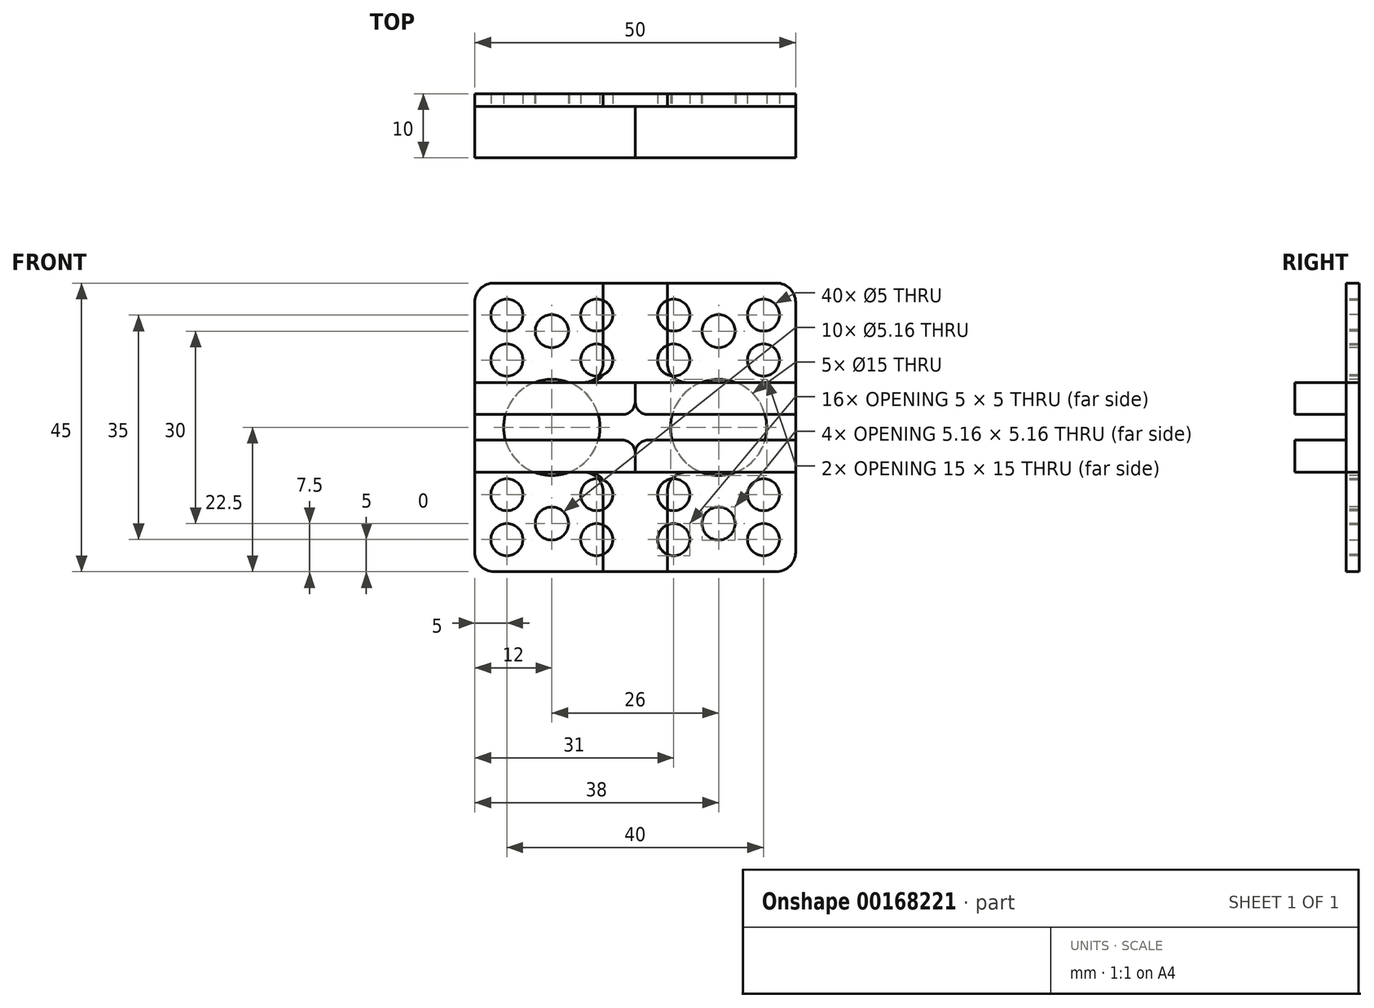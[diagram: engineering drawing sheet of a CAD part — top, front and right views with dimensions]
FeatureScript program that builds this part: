
annotation { "Feature Type Name" : "Feature", "Feature Type Description" : "" }
export const myFeature = defineFeature(function(context is Context, id is Id, definition is map)
    precondition{}
    {
        {
            var Q0;
            Q0=qCreatedBy(makeId("Top.planeOp"),FACE);
            var sketch = newSketch(context, id + "F0", { "sketchPlane" : qUnion([Q0])});
            skLineSegment(sketch, "E0.bottom", {"start": v(-25, -5) * mm, "end": v(25, -5) * mm});
            skLineSegment(sketch, "E0.top", {"start": v(-25, 5) * mm, "end": v(25, 5) * mm});
            skLineSegment(sketch, "E0.left", {"start": v(-25, -5) * mm, "end": v(-25, 5) * mm});
            skLineSegment(sketch, "E0.right", {"start": v(25, -5) * mm, "end": v(25, 5) * mm});
            skPoint(sketch, "E0.middle", {"position": v(0, 0) * mm});
            skSolve(sketch);
        }
        {
            var Q0;
            Q0 = qSketchRegion(id + "F0", true);
            extrude(context, id + "F1", {"entities" : qUnion([Q0]), "depth" : 45 * mm, "offsetDistance" : 25 * mm});
        }
        {
            var Q0;
            Q0=makeQuery(id+"F1.opExtrude","SWEPT_FACE",FACE,{"disambiguationData":[OSD([sQuery(id+"F0.wireOp",EDGE,"E0.bottom")])]});
            var sketch = newSketch(context, id + "F2", { "sketchPlane" : qUnion([Q0])});
            skCircle(sketch, "E1", {"center": v(13, 37.5) * mm, "radius": 2.58 * mm});
            skCircle(sketch, "E2", {"center": v(13, 7.5) * mm, "radius": 2.58 * mm});
            skLineSegment(sketch, "E3", {"start": v(13, 7.5) * mm, "end": v(13, 37.5) * mm, "construction": true});
            skLineSegment(sketch, "E4", {"start": v(13, 22.5) * mm, "end": v(25, 22.5) * mm, "construction": true});
            skSolve(sketch);
        }
        {
            var Q0;
            Q0 = qSketchRegion(id + "F2", true);
            extrude(context, id + "F3", {"entities" : qUnion([Q0]), "operationType" : NewBodyOperationType.REMOVE, "oppositeDirection" : true, "depth" : 25 * mm, "offsetDistance" : 25 * mm});
        }
        {
            var Q0;
            Q0=makeQuery(id+"F1.opExtrude","SWEPT_FACE",FACE,{"disambiguationData":[OSD([sQuery(id+"F0.wireOp",EDGE,"E0.bottom")])]});
            var sketch = newSketch(context, id + "F4", { "sketchPlane" : qUnion([Q0])});
            skCircle(sketch, "E5", {"center": v(13, 22.5) * mm, "radius": 7.5 * mm});
            skLineSegment(sketch, "E6", {"start": v(13, 7.5) * mm, "end": v(13, 22.5) * mm, "construction": true});
            skLineSegment(sketch, "E7", {"start": v(13, 37.5) * mm, "end": v(13, 22.5) * mm, "construction": true});
            skSolve(sketch);
        }
        {
            var Q0;
            Q0 = qSketchRegion(id + "F4", true);
            extrude(context, id + "F5", {"entities" : qUnion([Q0]), "operationType" : NewBodyOperationType.REMOVE, "endBound" : BoundingType.THROUGH_ALL, "oppositeDirection" : true, "depth" : 25 * mm, "offsetDistance" : 25 * mm});
        }
        {
            var Q0;
            Q0=makeQuery(id+"F1.opExtrude","SWEPT_FACE",FACE,{"disambiguationData":[OSD([sQuery(id+"F0.wireOp",EDGE,"E0.bottom")])]});
            var sketch = newSketch(context, id + "F6", { "sketchPlane" : qUnion([Q0])});
            skCircle(sketch, "E8", {"center": v(6, 5) * mm, "radius": 2.5 * mm});
            skLineSegment(sketch, "E9", {"start": v(13, 22.5) * mm, "end": v(-10.41, 22.5) * mm, "construction": true});
            skLineSegment(sketch, "E10", {"start": v(13, 22.5) * mm, "end": v(13, -17.77) * mm, "construction": true});
            skCircle(sketch, "E11.MirrorC", {"center": v(6, 40) * mm, "radius": 2.5 * mm});
            skCircle(sketch, "E12.MirrorC", {"center": v(20, 5) * mm, "radius": 2.5 * mm});
            skCircle(sketch, "E13.MirrorC", {"center": v(20, 40) * mm, "radius": 2.5 * mm});
            skCircle(sketch, "E14", {"center": v(6, 12) * mm, "radius": 2.5 * mm});
            skCircle(sketch, "E15.MirrorC", {"center": v(6, 33) * mm, "radius": 2.5 * mm});
            skCircle(sketch, "E16.MirrorC", {"center": v(20, 12) * mm, "radius": 2.5 * mm});
            skCircle(sketch, "E17.MirrorC", {"center": v(20, 33) * mm, "radius": 2.5 * mm});
            skSolve(sketch);
        }
        {
            var Q0;
            Q0 = qSketchRegion(id + "F6", true);
            extrude(context, id + "F7", {"entities" : qUnion([Q0]), "operationType" : NewBodyOperationType.REMOVE, "oppositeDirection" : true, "depth" : 25 * mm, "offsetDistance" : 25 * mm});
        }
        {
            var Q0;
            Q0=makeQuery(id+"F1.opExtrude","SWEPT_FACE",FACE,{"disambiguationData":[OSD([sQuery(id+"F0.wireOp",EDGE,"E0.bottom")])]});
            var sketch = newSketch(context, id + "F8", { "sketchPlane" : qUnion([Q0])});
            skLineSegment(sketch, "E18.bottom", {"start": v(-25, 24.5) * mm, "end": v(15, 24.5) * mm});
            skLineSegment(sketch, "E18.top", {"start": v(-25, 20.5) * mm, "end": v(15, 20.5) * mm});
            skLineSegment(sketch, "E18.left", {"start": v(-25, 24.5) * mm, "end": v(-25, 20.5) * mm});
            skLineSegment(sketch, "E18.right", {"start": v(15, 24.5) * mm, "end": v(15, 20.5) * mm});
            skLineSegment(sketch, "E19", {"start": v(15, 22.5) * mm, "end": v(25, 22.5) * mm, "construction": true});
            skLineSegment(sketch, "E20", {"start": v(25, 45) * mm, "end": v(25, 0) * mm});
            skLineSegment(sketch, "E21", {"start": v(25, 0) * mm, "end": v(-5, 0) * mm});
            skLineSegment(sketch, "E22", {"start": v(-5, 0) * mm, "end": v(-5, 15.5) * mm});
            skLineSegment(sketch, "E23", {"start": v(-5, 15.5) * mm, "end": v(-25, 15.5) * mm});
            skLineSegment(sketch, "E24", {"start": v(-25, 15.5) * mm, "end": v(-25, 20.5) * mm});
            skLineSegment(sketch, "E25", {"start": v(25, 45) * mm, "end": v(-5, 45) * mm});
            skLineSegment(sketch, "E26", {"start": v(-5, 45) * mm, "end": v(-5, 29.5) * mm});
            skLineSegment(sketch, "E27", {"start": v(-5, 29.5) * mm, "end": v(-25, 29.5) * mm});
            skLineSegment(sketch, "E28", {"start": v(-25, 29.5) * mm, "end": v(-25, 24.5) * mm});
            skLineSegment(sketch, "E29", {"start": v(-5, 29.5) * mm, "end": v(10.3, 29.5) * mm});
            skLineSegment(sketch, "E30", {"start": v(10.3, 29.5) * mm, "end": v(10.3, 15.5) * mm});
            skLineSegment(sketch, "E31", {"start": v(10.3, 15.5) * mm, "end": v(-5, 15.5) * mm});
            skLineSegment(sketch, "E32", {"start": v(0, 15.5) * mm, "end": v(0, 29.5) * mm});
            skPoint(sketch, "E33", {"position": v(2.65, 29.5) * mm});
            skSolve(sketch);
        }
        {
            var Q0;
            {var subQ0=sQuery(id+"F8.wireOp",EDGE,"E22");Q0=makeQuery(id+"F8.imprint","IMPRINT",FACE,{"disambiguationData":[TD([[makeQuery(id+"F8.imprint","IMPRINT",EDGE,{"derivedFrom":subQ0}),1.0]])]});}
            var Q1;
            {var subQ0=sQuery(id+"F8.wireOp",EDGE,"E26");Q1=makeQuery(id+"F8.imprint","IMPRINT",FACE,{"disambiguationData":[TD([[makeQuery(id+"F8.imprint","IMPRINT",EDGE,{"derivedFrom":subQ0}),-1.0]])]});}
            extrude(context, id + "F9", {"entities" : qUnion([Q0, Q1]), "operationType" : NewBodyOperationType.REMOVE, "oppositeDirection" : true, "depth" : 25 * mm, "offsetDistance" : 25 * mm});
        }
        {
            var Q0;
            Q0=makeQuery(id+"F8.imprint","IMPRINT",FACE,{"disambiguationData":[TD([[makeQuery(id+"F8.imprint","IMPRINT",EDGE,{"derivedFrom":sQuery(id+"F8.wireOp",EDGE,"E20")}),-1.0]])]});
            var Q1;
            {var subQ0=sQuery(id+"F8.wireOp",EDGE,"E18.left");Q1=makeQuery(id+"F8.imprint","IMPRINT",FACE,{"disambiguationData":[TD([[makeQuery(id+"F8.imprint","IMPRINT",EDGE,{"derivedFrom":subQ0}),1.0]])]});}
            var Q2;
            {var subQ0=sQuery(id+"F8.wireOp",EDGE,"E30");var subQ1=sQuery(id+"F8.wireOp",EDGE,"E18.bottom");var subQ2=makeQuery(id+"F8.imprint","INTERSECT",VERTEX,{"derivedFrom":[subQ1,subQ0]});Q2=makeQuery(id+"F8.imprint","IMPRINT",FACE,{"disambiguationData":[TD([[makeQuery(id+"F8.imprint","IMPRINT",EDGE,{"disambiguationData":[TD([[subQ2,1.0]])],"derivedFrom":subQ1}),-1.0]])]});}
            var Q3;
            {var subQ0=sQuery(id+"F8.wireOp",EDGE,"E32");var subQ1=sQuery(id+"F8.wireOp",EDGE,"E18.top");var subQ2=makeQuery(id+"F8.imprint","INTERSECT",VERTEX,{"derivedFrom":[subQ1,subQ0]});Q3=makeQuery(id+"F8.imprint","IMPRINT",FACE,{"disambiguationData":[TD([[makeQuery(id+"F8.imprint","IMPRINT",EDGE,{"disambiguationData":[TD([[subQ2,-1.0]])],"derivedFrom":subQ1}),-1.0]])]});}
            var Q4;
            {var subQ0=sQuery(id+"F8.wireOp",EDGE,"E32");var subQ1=sQuery(id+"F8.wireOp",EDGE,"E18.bottom");var subQ2=makeQuery(id+"F8.imprint","INTERSECT",VERTEX,{"derivedFrom":[subQ1,subQ0]});Q4=makeQuery(id+"F8.imprint","IMPRINT",FACE,{"disambiguationData":[TD([[makeQuery(id+"F8.imprint","IMPRINT",EDGE,{"disambiguationData":[TD([[subQ2,-1.0]])],"derivedFrom":subQ1}),-1.0]])]});}
            var Q5;
            {var subQ0=sQuery(id+"F8.wireOp",EDGE,"E32");var subQ1=sQuery(id+"F8.wireOp",EDGE,"E18.bottom");var subQ2=makeQuery(id+"F8.imprint","INTERSECT",VERTEX,{"derivedFrom":[subQ1,subQ0]});Q5=makeQuery(id+"F8.imprint","IMPRINT",FACE,{"disambiguationData":[TD([[makeQuery(id+"F8.imprint","IMPRINT",EDGE,{"disambiguationData":[TD([[subQ2,-1.0]])],"derivedFrom":subQ1}),1.0]])]});}
            extrude(context, id + "F10", {"entities" : qUnion([Q0, Q1, Q2, Q3, Q4, Q5]), "operationType" : NewBodyOperationType.REMOVE, "oppositeDirection" : true, "depth" : 8 * mm, "offsetDistance" : 25 * mm});
        }
        {
            var Q0;
            Q0=makeQuery(id+"F1.opExtrude","CAP_EDGE",EDGE,{"disambiguationData":[OSD([sQuery(id+"F0.wireOp",EDGE,"E0.right")])],"isStart":true});
            var Q1;
            Q1=makeQuery(id+"F1.opExtrude","CAP_EDGE",EDGE,{"disambiguationData":[OSD([sQuery(id+"F0.wireOp",EDGE,"E0.right")])],"isStart":false});
            var Q2;
            Q2=makeQuery(id+"F9.boolean.opBoolean","COPY",EDGE,{"derivedFrom":makeQuery(id+"F9.opExtrude","SWEPT_EDGE",EDGE,{"disambiguationData":[OSD([sQuery(id+"F0.wireOp",EDGE,"E0.bottom"),sQuery(id+"F8.wireOp",EDGE,"E25"),sQuery(id+"F8.wireOp",EDGE,"E26")])]})});
            var Q3;
            Q3=makeQuery(id+"F9.boolean.opBoolean","COPY",EDGE,{"derivedFrom":makeQuery(id+"F9.opExtrude","SWEPT_EDGE",EDGE,{"disambiguationData":[OSD([sQuery(id+"F8.wireOp",EDGE,"E26"),sQuery(id+"F8.wireOp",EDGE,"E27"),sQuery(id+"F8.wireOp",EDGE,"E29")])]})});
            var Q4;
            Q4=makeQuery(id+"F9.boolean.opBoolean","COPY",EDGE,{"derivedFrom":makeQuery(id+"F9.opExtrude","SWEPT_EDGE",EDGE,{"disambiguationData":[OSD([sQuery(id+"F0.wireOp",EDGE,"E0.bottom"),sQuery(id+"F8.wireOp",EDGE,"E21"),sQuery(id+"F8.wireOp",EDGE,"E22")])]})});
            var Q5;
            Q5=makeQuery(id+"F9.boolean.opBoolean","COPY",EDGE,{"derivedFrom":makeQuery(id+"F9.opExtrude","SWEPT_EDGE",EDGE,{"disambiguationData":[OSD([sQuery(id+"F8.wireOp",EDGE,"E22"),sQuery(id+"F8.wireOp",EDGE,"E23"),sQuery(id+"F8.wireOp",EDGE,"E31")])]})});
            fillet(context, id + "F11", {"entities" : qUnion([Q0, Q1, Q2, Q3, Q4, Q5]), "radius" : 3 * mm, "tangentPropagation" : true, "allowEdgeOverflow" : false});
        }
        {
            var Q0;
            Q0=makeQuery(id+"F10.boolean.opBoolean","COPY",EDGE,{"derivedFrom":makeQuery(id+"F10.opExtrude","SWEPT_EDGE",EDGE,{"disambiguationData":[OSD([sQuery(id+"F8.wireOp",EDGE,"E18.top"),sQuery(id+"F8.wireOp",EDGE,"E32")])]})});
            var Q1;
            Q1=makeQuery(id+"F10.boolean.opBoolean","COPY",EDGE,{"derivedFrom":makeQuery(id+"F10.opExtrude","SWEPT_EDGE",EDGE,{"disambiguationData":[OSD([sQuery(id+"F8.wireOp",EDGE,"E18.bottom"),sQuery(id+"F8.wireOp",EDGE,"E32")])]})});
            fillet(context, id + "F12", {"entities" : qUnion([Q0, Q1]), "radius" : 2 * mm, "tangentPropagation" : true, "allowEdgeOverflow" : false});
        }
        {
            var Q0;
            Q0=makeQuery(id+"F1.opExtrude","SWEPT_BODY",BODY,{"disambiguationData":[OSD([sQuery(id+"F0.wireOp",EDGE,"E0.bottom"),sQuery(id+"F0.wireOp",EDGE,"E0.top"),sQuery(id+"F0.wireOp",EDGE,"E0.left"),sQuery(id+"F0.wireOp",EDGE,"E0.right")])]});
            var Q1;
            Q1=qCreatedBy(makeId("Right.planeOp"),FACE);
            mirror(context, id + "F13", {"entities" : qUnion([Q0]), "mirrorPlane" : qUnion([Q1])});
        }
    });
